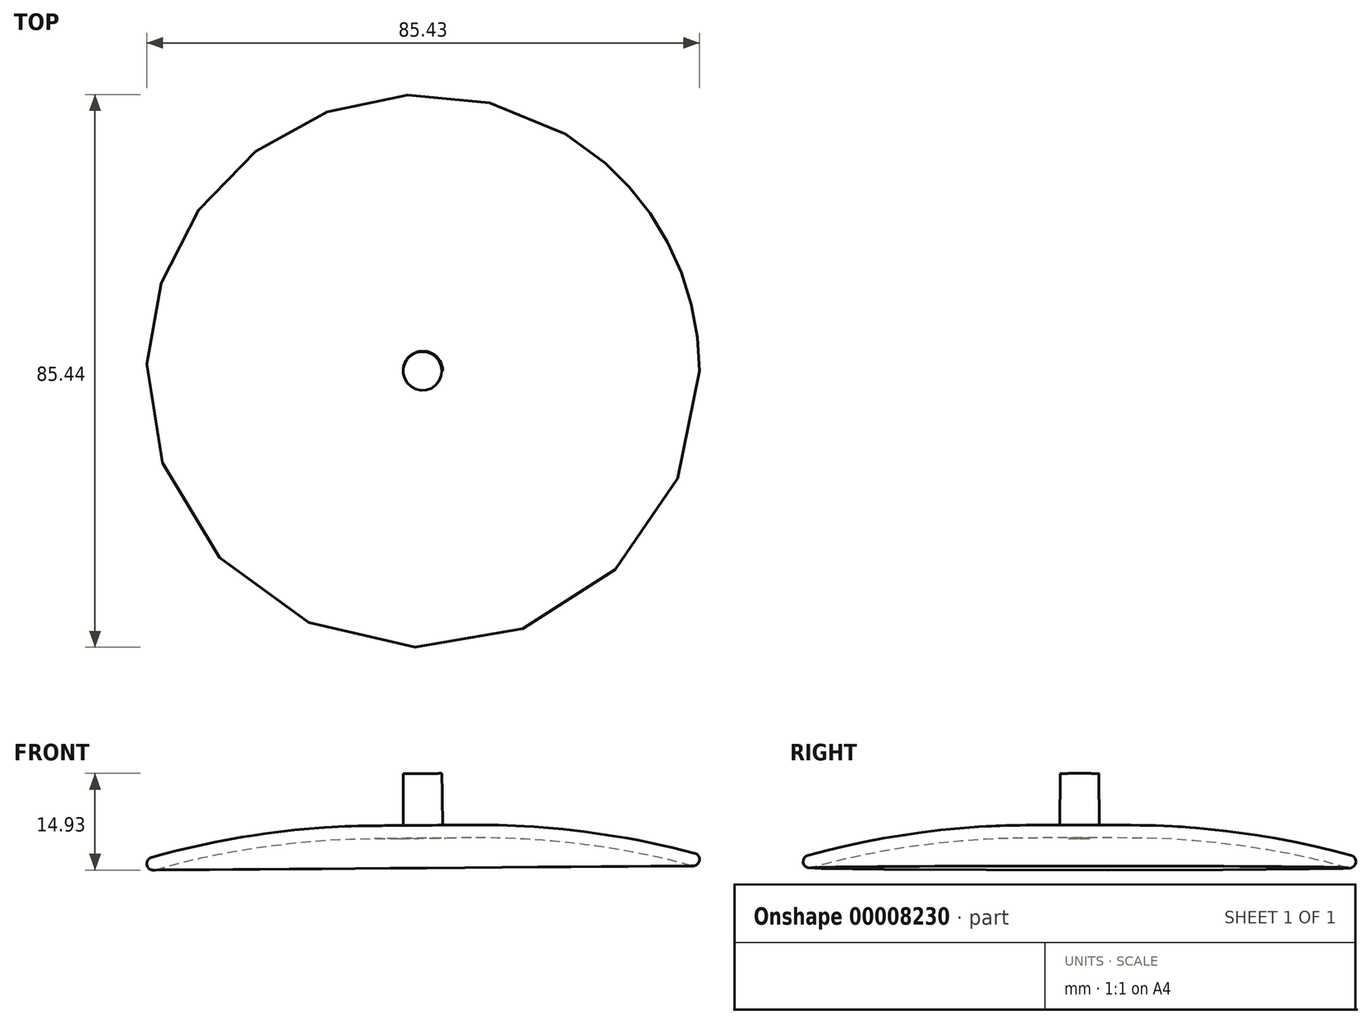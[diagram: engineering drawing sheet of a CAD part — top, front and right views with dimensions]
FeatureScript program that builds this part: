
annotation { "Feature Type Name" : "Feature", "Feature Type Description" : "" }
export const myFeature = defineFeature(function(context is Context, id is Id, definition is map)
    precondition{}
    {
        {
            var Q0;
            Q0=qCreatedBy(makeId("Front.planeOp"),FACE);
            var sketch = newSketch(context, id + "F0", { "sketchPlane" : qUnion([Q0])});
            skFitSpline(sketch, "E0", {"points": [v(-41.88, 0) * mm, v(-14.1, 4.7) * mm, v(0, 5) * mm], "startDerivative": vector(50.54, 14.37) * mm, "endDerivative": vector(32.24, 1.23) * mm});
            skFitSpline(sketch, "E1.0", {"points": [v(-41.34, -1.92) * mm, v(-39.27, -1.34) * mm, v(-35.1, -0.28) * mm, v(-28.9, 0.96) * mm, v(-23.92, 1.72) * mm, v(-20.14, 2.18) * mm, v(-17.43, 2.45) * mm, v(-14.86, 2.65) * mm, v(-12.47, 2.78) * mm, v(-10.22, 2.85) * mm, v(-7.36, 2.9) * mm, v(-3.98, 2.9) * mm, v(-1.3, 2.95) * mm, v(0.08, 3) * mm]});
            skArc(sketch, "E2", {"start": v(-41.88, 0) * mm, "mid": v(-42.57, -1.24) * mm, "end": v(-41.34, -1.92) * mm});
            skLineSegment(sketch, "E3", {"start": v(-3, 4.93) * mm, "end": v(-3, 12.93) * mm});
            skLineSegment(sketch, "E4", {"start": v(-3, 12.93) * mm, "end": v(0, 12.93) * mm});
            skLineSegment(sketch, "E5", {"start": v(0, 12.93) * mm, "end": v(0.08, 3) * mm});
            skLineSegment(sketch, "E6", {"start": v(0, 0) * mm, "end": v(0, -9.68) * mm, "construction": true});
            skSolve(sketch);
        }
        {
            var Q0;
            Q0=makeQuery(id+"F0.imprint","IMPRINT",FACE,{"disambiguationData":[TD([[makeQuery(id+"F0.imprint","IMPRINT",EDGE,{"derivedFrom":sQuery(id+"F0.wireOp",EDGE,"E0")}),-1.0]])]});
            var Q1;
            Q1=sQuery(id+"F0.wireOp",EDGE,"E5");
            revolve(context, id + "F1", {"entities" : qUnion([Q0]), "axis" : qUnion([Q1]), "revolveType" : RevolveType.FULL});
        }
    });
